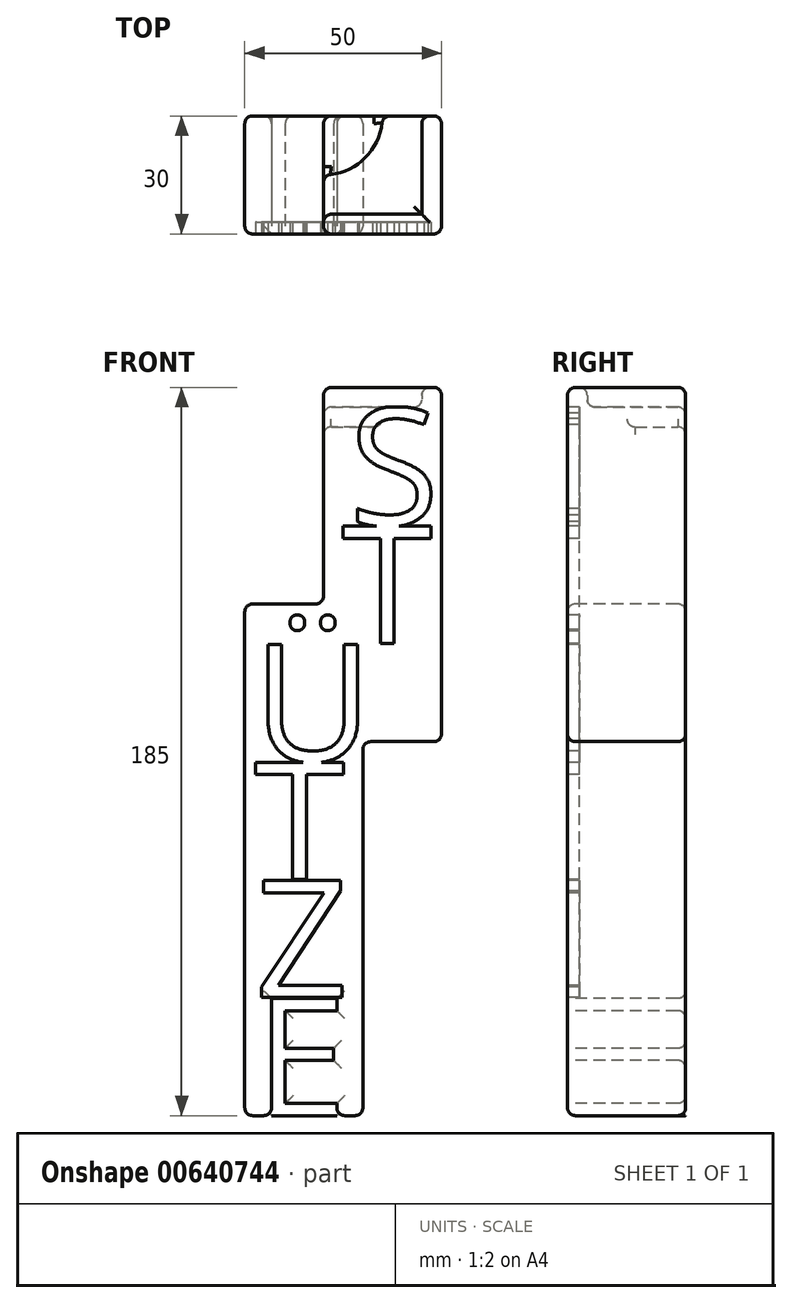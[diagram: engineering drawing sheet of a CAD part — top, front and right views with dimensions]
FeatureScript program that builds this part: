
annotation { "Feature Type Name" : "Feature", "Feature Type Description" : "" }
export const myFeature = defineFeature(function(context is Context, id is Id, definition is map)
    precondition{}
    {
        {
            var Q0;
            Q0=qCreatedBy(makeId("Front.planeOp"),FACE);
            var sketch = newSketch(context, id + "F0", { "sketchPlane" : qUnion([Q0])});
            skText(sketch, "E0", { "text": "S", "fontName": "OpenSans-Regular.ttf"});
            skText(sketch, "E1", { "text": "T", "fontName": "OpenSans-Regular.ttf"});
            skText(sketch, "E2", { "text": "Ü", "fontName": "OpenSans-Regular.ttf"});
            skText(sketch, "E3", { "text": "T", "fontName": "OpenSans-Regular.ttf"});
            skText(sketch, "E4", { "text": "Z", "fontName": "OpenSans-Regular.ttf"});
            skText(sketch, "E5", { "text": "E", "fontName": "OpenSans-Regular.ttf"});
            skLineSegment(sketch, "E6.bottom", {"start": v(-30, 75.9) * mm, "end": v(0, 75.9) * mm});
            skLineSegment(sketch, "E6.top", {"start": v(-50, -104.1) * mm, "end": v(-20, -104.1) * mm});
            skLineSegment(sketch, "E6.left", {"start": v(-50, 25.9) * mm, "end": v(-50, -104.1) * mm});
            skLineSegment(sketch, "E6.right", {"start": v(0, 75.9) * mm, "end": v(0, -9.1) * mm});
            skLineSegment(sketch, "E7.top", {"start": v(0, -9.1) * mm, "end": v(-20, -9.1) * mm});
            skLineSegment(sketch, "E7.right", {"start": v(-20, -104.1) * mm, "end": v(-20, -9.1) * mm});
            skLineSegment(sketch, "E8.top", {"start": v(-50, 25.9) * mm, "end": v(-30, 25.9) * mm});
            skLineSegment(sketch, "E8.right", {"start": v(-30, 75.9) * mm, "end": v(-30, 25.9) * mm});
            skLineSegment(sketch, "E9.top", {"start": v(-30, 80.9) * mm, "end": v(0, 80.9) * mm});
            skLineSegment(sketch, "E9.left", {"start": v(-30, 75.9) * mm, "end": v(-30, 80.9) * mm});
            skLineSegment(sketch, "E9.right", {"start": v(0, 75.9) * mm, "end": v(0, 80.9) * mm});
            const initialGuessF0  = {"E0": [-0.02357, 0.0459, 1, 0, 0.03], "E1": [-0.02536, 0.0159, 1, 0, 0.03], "E2": [-0.04788, -0.0141, 1, 0, 0.03], "E3": [-0.04761, -0.0441, 1, 0, 0.03], "E4": [-0.04735, -0.0741, 1, 0, 0.03], "E5": [-0.04727, -0.1041, 1, 0, 0.03]};
            skSetInitialGuess(sketch, initialGuessF0);
            skSolve(sketch);
        }
        {
            var Q0;
            {var subQ0=sQuery(id+"F0.wireOp",EDGE,"E5.sketch_text.stroke-1");Q0=makeQuery(id+"F0.imprint","IMPRINT",FACE,{"disambiguationData":[TD([[makeQuery(id+"F0.imprint","IMPRINT",EDGE,{"derivedFrom":subQ0}),-1.0]])]});}
            var Q1;
            {var subQ21=sQuery(id+"F0.wireOp",EDGE,"E0.sketch_text.stroke-0");Q1=makeQuery(id+"F0.imprint","IMPRINT",FACE,{"disambiguationData":[TD([[makeQuery(id+"F0.imprint","IMPRINT",EDGE,{"derivedFrom":subQ21}),1.0]])]});}
            var Q2;
            Q2=makeQuery(id+"F0.imprint","IMPRINT",FACE,{"disambiguationData":[TD([[makeQuery(id+"F0.imprint","IMPRINT",EDGE,{"derivedFrom":sQuery(id+"F0.wireOp",EDGE,"E1.sketch_text.stroke-0")}),-1.0]])]});
            var Q3;
            Q3=makeQuery(id+"F0.imprint","IMPRINT",FACE,{"disambiguationData":[TD([[makeQuery(id+"F0.imprint","IMPRINT",EDGE,{"derivedFrom":sQuery(id+"F0.wireOp",EDGE,"E2.sketch_text.stroke-14")}),-1.0]])]});
            var Q4;
            Q4=makeQuery(id+"F0.imprint","IMPRINT",FACE,{"disambiguationData":[TD([[makeQuery(id+"F0.imprint","IMPRINT",EDGE,{"derivedFrom":sQuery(id+"F0.wireOp",EDGE,"E2.sketch_text.stroke-22")}),-1.0]])]});
            var Q5;
            Q5=makeQuery(id+"F0.imprint","IMPRINT",FACE,{"disambiguationData":[TD([[makeQuery(id+"F0.imprint","IMPRINT",EDGE,{"derivedFrom":sQuery(id+"F0.wireOp",EDGE,"E2.sketch_text.stroke-0")}),-1.0]])]});
            var Q6;
            Q6=makeQuery(id+"F0.imprint","IMPRINT",FACE,{"disambiguationData":[TD([[makeQuery(id+"F0.imprint","IMPRINT",EDGE,{"derivedFrom":sQuery(id+"F0.wireOp",EDGE,"E3.sketch_text.stroke-0")}),-1.0]])]});
            var Q7;
            Q7=makeQuery(id+"F0.imprint","IMPRINT",FACE,{"disambiguationData":[TD([[makeQuery(id+"F0.imprint","IMPRINT",EDGE,{"derivedFrom":sQuery(id+"F0.wireOp",EDGE,"E4.sketch_text.stroke-0")}),-1.0]])]});
            var Q8;
            {var subQ0=sQuery(id+"F0.wireOp",EDGE,"E0.sketch_text.stroke-2");var subQ1=sQuery(id+"F0.wireOp",EDGE,"E0.sketch_text.stroke-1");var subQ2=makeQuery(id+"F0.imprint","INTERSECT",VERTEX,{"derivedFrom":[subQ1,subQ0]});Q8=makeQuery(id+"F0.imprint","IMPRINT",FACE,{"disambiguationData":[TD([[makeQuery(id+"F0.imprint","IMPRINT",EDGE,{"disambiguationData":[TD([[subQ2,1.0]])],"derivedFrom":subQ1}),-1.0]])]});}
            var Q9;
            {var subQ0=sQuery(id+"F0.wireOp",EDGE,"E2.sketch_text.stroke-3");var subQ1=sQuery(id+"F0.wireOp",EDGE,"E2.sketch_text.stroke-2");var subQ2=makeQuery(id+"F0.imprint","INTERSECT",VERTEX,{"derivedFrom":[subQ1,subQ0]});Q9=makeQuery(id+"F0.imprint","IMPRINT",FACE,{"disambiguationData":[TD([[makeQuery(id+"F0.imprint","IMPRINT",EDGE,{"disambiguationData":[TD([[subQ2,1.0]])],"derivedFrom":subQ1}),-1.0]])]});}
            var Q10;
            {var subQ12=sQuery(id+"F0.wireOp",EDGE,"E0.sketch_text.stroke-0");Q10=makeQuery(id+"F0.imprint","IMPRINT",FACE,{"disambiguationData":[TD([[makeQuery(id+"F0.imprint","IMPRINT",EDGE,{"derivedFrom":subQ12}),-1.0]])]});}
            extrude(context, id + "F1", {"entities" : qUnion([Q0, Q1, Q2, Q3, Q4, Q5, Q6, Q7, Q8, Q9, Q10]), "oppositeDirection" : true, "depth" : 30 * mm, "offsetDistance" : 25 * mm});
        }
        {
            var Q0;
            {var subQ0=sQuery(id+"F0.wireOp",EDGE,"E0.sketch_text.stroke-15");var subQ1=sQuery(id+"F0.wireOp",EDGE,"E0.sketch_text.stroke-14");var subQ2=makeQuery(id+"F0.imprint","INTERSECT",VERTEX,{"derivedFrom":[subQ1,subQ0]});Q0=makeQuery(id+"F0.imprint","IMPRINT",FACE,{"disambiguationData":[TD([[makeQuery(id+"F0.imprint","IMPRINT",EDGE,{"disambiguationData":[TD([[subQ2,1.0]])],"derivedFrom":subQ1}),-1.0]])]});}
            var Q1;
            {var subQ0=sQuery(id+"F0.wireOp",EDGE,"E5.sketch_text.stroke-1");Q1=makeQuery(id+"F0.imprint","IMPRINT",FACE,{"disambiguationData":[TD([[makeQuery(id+"F0.imprint","IMPRINT",EDGE,{"derivedFrom":subQ0}),-1.0]])]});}
            var Q2;
            Q2=makeQuery(id+"F0.imprint","IMPRINT",FACE,{"disambiguationData":[TD([[makeQuery(id+"F0.imprint","IMPRINT",EDGE,{"derivedFrom":sQuery(id+"F0.wireOp",EDGE,"E1.sketch_text.stroke-0")}),-1.0]])]});
            var Q3;
            {var subQ0=sQuery(id+"F0.wireOp",EDGE,"E0.sketch_text.stroke-2");var subQ1=sQuery(id+"F0.wireOp",EDGE,"E0.sketch_text.stroke-1");var subQ2=makeQuery(id+"F0.imprint","INTERSECT",VERTEX,{"derivedFrom":[subQ1,subQ0]});Q3=makeQuery(id+"F0.imprint","IMPRINT",FACE,{"disambiguationData":[TD([[makeQuery(id+"F0.imprint","IMPRINT",EDGE,{"disambiguationData":[TD([[subQ2,1.0]])],"derivedFrom":subQ1}),-1.0]])]});}
            var Q4;
            {var subQ12=sQuery(id+"F0.wireOp",EDGE,"E0.sketch_text.stroke-0");Q4=makeQuery(id+"F0.imprint","IMPRINT",FACE,{"disambiguationData":[TD([[makeQuery(id+"F0.imprint","IMPRINT",EDGE,{"derivedFrom":subQ12}),-1.0]])]});}
            var Q5;
            Q5=makeQuery(id+"F0.imprint","IMPRINT",FACE,{"disambiguationData":[TD([[makeQuery(id+"F0.imprint","IMPRINT",EDGE,{"derivedFrom":sQuery(id+"F0.wireOp",EDGE,"E2.sketch_text.stroke-14")}),-1.0]])]});
            var Q6;
            Q6=makeQuery(id+"F0.imprint","IMPRINT",FACE,{"disambiguationData":[TD([[makeQuery(id+"F0.imprint","IMPRINT",EDGE,{"derivedFrom":sQuery(id+"F0.wireOp",EDGE,"E2.sketch_text.stroke-22")}),-1.0]])]});
            var Q7;
            Q7=makeQuery(id+"F0.imprint","IMPRINT",FACE,{"disambiguationData":[TD([[makeQuery(id+"F0.imprint","IMPRINT",EDGE,{"derivedFrom":sQuery(id+"F0.wireOp",EDGE,"E3.sketch_text.stroke-0")}),-1.0]])]});
            var Q8;
            {var subQ0=sQuery(id+"F0.wireOp",EDGE,"E2.sketch_text.stroke-3");var subQ1=sQuery(id+"F0.wireOp",EDGE,"E2.sketch_text.stroke-2");var subQ2=makeQuery(id+"F0.imprint","INTERSECT",VERTEX,{"derivedFrom":[subQ1,subQ0]});Q8=makeQuery(id+"F0.imprint","IMPRINT",FACE,{"disambiguationData":[TD([[makeQuery(id+"F0.imprint","IMPRINT",EDGE,{"disambiguationData":[TD([[subQ2,1.0]])],"derivedFrom":subQ1}),-1.0]])]});}
            var Q9;
            Q9=makeQuery(id+"F0.imprint","IMPRINT",FACE,{"disambiguationData":[TD([[makeQuery(id+"F0.imprint","IMPRINT",EDGE,{"derivedFrom":sQuery(id+"F0.wireOp",EDGE,"E2.sketch_text.stroke-0")}),-1.0]])]});
            var Q10;
            Q10=makeQuery(id+"F0.imprint","IMPRINT",FACE,{"disambiguationData":[TD([[makeQuery(id+"F0.imprint","IMPRINT",EDGE,{"derivedFrom":sQuery(id+"F0.wireOp",EDGE,"E4.sketch_text.stroke-0")}),-1.0]])]});
            extrude(context, id + "F2", {"entities" : qUnion([Q0, Q1, Q2, Q3, Q4, Q5, Q6, Q7, Q8, Q9, Q10]), "operationType" : NewBodyOperationType.REMOVE, "oppositeDirection" : true, "depth" : 3 * mm, "offsetDistance" : 25 * mm});
        }
        {
            var Q0;
            {var subQ0=sQuery(id+"F0.wireOp",EDGE,"E0.sketch_text.stroke-15");var subQ1=sQuery(id+"F0.wireOp",EDGE,"E0.sketch_text.stroke-14");var subQ2=makeQuery(id+"F0.imprint","INTERSECT",VERTEX,{"derivedFrom":[subQ1,subQ0]});Q0=makeQuery(id+"F0.imprint","IMPRINT",FACE,{"disambiguationData":[TD([[makeQuery(id+"F0.imprint","IMPRINT",EDGE,{"disambiguationData":[TD([[subQ2,1.0]])],"derivedFrom":subQ1}),-1.0]])]});}
            var Q1;
            Q1=makeQuery(id+"F0.imprint","IMPRINT",FACE,{"disambiguationData":[TD([[makeQuery(id+"F0.imprint","IMPRINT",EDGE,{"derivedFrom":sQuery(id+"F0.wireOp",EDGE,"E9.top")}),-1.0]])]});
            extrude(context, id + "F3", {"entities" : qUnion([Q0, Q1]), "operationType" : NewBodyOperationType.ADD, "oppositeDirection" : true, "depth" : 5 * mm, "offsetDistance" : 25 * mm});
        }
        {
            var Q0;
            Q0=qCreatedBy(makeId("Right.planeOp"),FACE);
            var sketch = newSketch(context, id + "F4", { "sketchPlane" : qUnion([Q0])});
            skLineSegment(sketch, "E10.bottom", {"start": v(5, 80.9) * mm, "end": v(30, 80.9) * mm});
            skLineSegment(sketch, "E10.top", {"start": v(5, 75.9) * mm, "end": v(30, 75.9) * mm});
            skLineSegment(sketch, "E10.left", {"start": v(5, 80.9) * mm, "end": v(5, 75.9) * mm});
            skLineSegment(sketch, "E10.right", {"start": v(30, 80.9) * mm, "end": v(30, 75.9) * mm});
            skSolve(sketch);
        }
        {
            var Q0;
            Q0 = qSketchRegion(id + "F4", true);
            var Q1;
            Q1=makeQuery(id+"F4.imprint","IMPRINT",FACE,{"disambiguationData":[TD([[makeQuery(id+"F4.imprint","IMPRINT",EDGE,{"derivedFrom":sQuery(id+"F4.wireOp",EDGE,"E10.bottom")}),-1.0]])]});
            extrude(context, id + "F5", {"entities" : qUnion([Q0, Q1]), "operationType" : NewBodyOperationType.ADD, "oppositeDirection" : true, "depth" : 5 * mm, "offsetDistance" : 25 * mm});
        }
        {
            var Q0;
            Q0=makeQuery(id+"F1.opExtrude","SWEPT_FACE",FACE,{"disambiguationData":[OSD([sQuery(id+"F0.wireOp",EDGE,"E6.bottom")])]});
            var sketch = newSketch(context, id + "F6", { "sketchPlane" : qUnion([Q0])});
            skCircle(sketch, "E11", {"center": v(-30, 30) * mm, "radius": 15 * mm});
            skSolve(sketch);
        }
        {
            var Q0;
            Q0 = qSketchRegion(id + "F6", true);
            extrude(context, id + "F7", {"entities" : qUnion([Q0]), "operationType" : NewBodyOperationType.REMOVE, "oppositeDirection" : true, "depth" : 5 * mm, "offsetDistance" : 25 * mm});
        }
        {
            var Q0;
            Q0=makeQuery(id+"F5.boolean.opBoolean","MERGE",FACE,{"derivedFrom":[makeQuery(id+"F3.boolean.opBoolean","MERGE",FACE,{"derivedFrom":[makeQuery(id+"F1.opExtrude","SWEPT_FACE",FACE,{"disambiguationData":[OSD([sQuery(id+"F0.wireOp",EDGE,"E6.right")])]}),makeQuery(id+"F3.opExtrude","SWEPT_FACE",FACE,{"disambiguationData":[OSD([sQuery(id+"F0.wireOp",EDGE,"E9.right")])]})]}),makeQuery(id+"F5.opExtrude","CAP_FACE",FACE,{"disambiguationData":[OSD([sQuery(id+"F4.wireOp",EDGE,"E10.bottom"),sQuery(id+"F4.wireOp",EDGE,"E10.top"),sQuery(id+"F4.wireOp",EDGE,"E10.left"),sQuery(id+"F4.wireOp",EDGE,"E10.right")])],"isStart":true})]});
            var Q1;
            Q1=makeQuery(id+"F5.opExtrude","CAP_EDGE",EDGE,{"disambiguationData":[OSD([sQuery(id+"F4.wireOp",EDGE,"E10.bottom")])],"isStart":false});
            var Q2;
            Q2=makeQuery(id+"F3.opExtrude","CAP_EDGE",EDGE,{"disambiguationData":[OSD([sQuery(id+"F0.wireOp",EDGE,"E9.top")])],"isStart":true});
            var Q3;
            Q3=makeQuery(id+"F5.boolean.opBoolean","MERGE",EDGE,{"derivedFrom":[makeQuery(id+"F3.opExtrude","SWEPT_EDGE",EDGE,{"disambiguationData":[OSD([sQuery(id+"F0.wireOp",EDGE,"E9.top"),sQuery(id+"F0.wireOp",EDGE,"E9.right")])]}),makeQuery(id+"F5.opExtrude","CAP_EDGE",EDGE,{"disambiguationData":[OSD([sQuery(id+"F4.wireOp",EDGE,"E10.bottom")])],"isStart":true})]});
            var Q4;
            Q4=makeQuery(id+"F5.opExtrude","SWEPT_EDGE",EDGE,{"disambiguationData":[OSD([sQuery(id+"F4.wireOp",EDGE,"E10.bottom"),sQuery(id+"F4.wireOp",EDGE,"E10.right")])]});
            var Q5;
            Q5=makeQuery(id+"F3.opExtrude","CAP_EDGE",EDGE,{"disambiguationData":[OSD([sQuery(id+"F0.wireOp",EDGE,"E9.top")])],"isStart":false});
            var Q6;
            Q6=makeQuery(id+"F3.opExtrude","SWEPT_EDGE",EDGE,{"disambiguationData":[OSD([sQuery(id+"F0.wireOp",EDGE,"E9.top"),sQuery(id+"F0.wireOp",EDGE,"E9.left")])]});
            var Q7;
            Q7=makeQuery(id+"F1.opExtrude","SWEPT_EDGE",EDGE,{"disambiguationData":[OSD([sQuery(id+"F0.wireOp",EDGE,"E8.right"),sQuery(id+"F0.wireOp",EDGE,"E6.bottom"),sQuery(id+"F0.wireOp",EDGE,"E9.left")])]});
            var Q8;
            Q8=makeQuery(id+"F5.boolean.opBoolean","MERGE",FACE,{"derivedFrom":[makeQuery(id+"F1.opExtrude","CAP_FACE",FACE,{"disambiguationData":[OSD([sQuery(id+"F0.wireOp",EDGE,"E6.top"),sQuery(id+"F0.wireOp",EDGE,"E6.left"),sQuery(id+"F0.wireOp",EDGE,"E6.right"),sQuery(id+"F0.wireOp",EDGE,"E7.top"),sQuery(id+"F0.wireOp",EDGE,"E7.right"),sQuery(id+"F0.wireOp",EDGE,"E8.top"),sQuery(id+"F0.wireOp",EDGE,"E8.right"),sQuery(id+"F0.wireOp",EDGE,"E6.bottom")])],"isStart":false}),makeQuery(id+"F5.opExtrude","SWEPT_FACE",FACE,{"disambiguationData":[OSD([sQuery(id+"F4.wireOp",EDGE,"E10.right")])]})]});
            var Q9;
            Q9=makeQuery(id+"F3.boolean.opBoolean","MERGE",FACE,{"derivedFrom":[makeQuery(id+"F1.opExtrude","SWEPT_FACE",FACE,{"disambiguationData":[OSD([sQuery(id+"F0.wireOp",EDGE,"E8.right")])]}),makeQuery(id+"F3.opExtrude","SWEPT_FACE",FACE,{"disambiguationData":[OSD([sQuery(id+"F0.wireOp",EDGE,"E9.left")])]})]});
            var Q10;
            Q10=makeQuery(id+"F1.opExtrude","SWEPT_FACE",FACE,{"disambiguationData":[OSD([sQuery(id+"F0.wireOp",EDGE,"E6.bottom")])]});
            var Q11;
            Q11=makeQuery(id+"F1.opExtrude","SWEPT_EDGE",EDGE,{"disambiguationData":[OSD([sQuery(id+"F0.wireOp",EDGE,"E6.left"),sQuery(id+"F0.wireOp",EDGE,"E8.top")])]});
            var Q12;
            Q12=makeQuery(id+"F1.opExtrude","SWEPT_EDGE",EDGE,{"disambiguationData":[OSD([sQuery(id+"F0.wireOp",EDGE,"E8.top"),sQuery(id+"F0.wireOp",EDGE,"E8.right")])]});
            var Q13;
            Q13=makeQuery(id+"F1.opExtrude","SWEPT_FACE",FACE,{"disambiguationData":[OSD([sQuery(id+"F0.wireOp",EDGE,"E8.top")])]});
            var Q14;
            Q14=makeQuery(id+"F1.opExtrude","SWEPT_FACE",FACE,{"disambiguationData":[OSD([sQuery(id+"F0.wireOp",EDGE,"E7.top")])]});
            var Q15;
            Q15=makeQuery(id+"F1.opExtrude","SWEPT_FACE",FACE,{"disambiguationData":[OSD([sQuery(id+"F0.wireOp",EDGE,"E7.right")])]});
            var Q16;
            Q16=makeQuery(id+"F1.opExtrude","SWEPT_EDGE",EDGE,{"disambiguationData":[OSD([sQuery(id+"F0.wireOp",EDGE,"E6.top"),sQuery(id+"F0.wireOp",EDGE,"E6.left")])]});
            var Q17;
            {var subQ0=sQuery(id+"F0.wireOp",EDGE,"E6.top");Q17=makeQuery(id+"F2.boolean.opBoolean","MERGE",FACE,{"derivedFrom":[makeQuery(id+"F1.opExtrude","SWEPT_FACE",FACE,{"disambiguationData":[OSD([subQ0])]}),makeQuery(id+"F2.opExtrude","SWEPT_FACE",FACE,{"disambiguationData":[OSD([subQ0])]})]});}
            var Q18;
            Q18=makeQuery(id+"F1.opExtrude","SWEPT_FACE",FACE,{"disambiguationData":[OSD([sQuery(id+"F0.wireOp",EDGE,"E6.left")])]});
            var Q19;
            Q19=makeQuery(id+"F7.boolean.opBoolean","COPY",FACE,{"derivedFrom":makeQuery(id+"F7.opExtrude","CAP_FACE",FACE,{"disambiguationData":[OSD([sQuery(id+"F6.wireOp",EDGE,"E11")])],"isStart":false})});
            fillet(context, id + "F8", {"entities" : qUnion([Q0, Q1, Q2, Q3, Q4, Q5, Q6, Q7, Q8, Q9, Q10, Q11, Q12, Q13, Q14, Q15, Q16, Q17, Q18, Q19]), "radius" : 2 * mm, "tangentPropagation" : true, "allowEdgeOverflow" : false});
        }
    });
